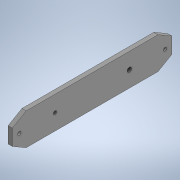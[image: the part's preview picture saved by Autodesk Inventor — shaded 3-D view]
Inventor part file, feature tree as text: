
AUTODESK INVENTOR PART (.ipt)
format: ipt  version: 2020 (Build 240168000, 168)  size: 168,448 bytes
history: native  units: in
note: dims shown in document units (in); Inventor stores cm internally (conversion verified against a paired STEP export)
features: other x3, extrude x3, sketch x3, projected_geometry x1
ambient origin geometry x8: Origin, YZ Plane, XZ Plane, XY Plane, X Axis, Y Axis, Z Axis, Center Point
bodies: Solid1 (feature_tree)
feature tree (10):
  other  "HexWheelGuard.ipt"
  extrude  "Extrusion1"  TaperAngle=0.0deg  [1 undecoded]
  extrude  "Extrusion2"  Depth=0.3937in
  extrude  "Extrusion3"  Depth=0.3937in TaperAngle=0.0deg
  other  "Solid1::HexWheelGuard.ipt"
  other  "TaggingFeature1"
  sketch  "Sketch1"  dims[d0=0.3937in d1=0.0in d2=0.0in]
  projected_geometry  "Projected Loop1"
  sketch  "Sketch2"  dims[d3=0.3937in d4=0.0in d5=0.122in]
  sketch  "Sketch3"  dims[d6=0.122in d7=0.3937in d8=0.0in]
note: 1 required parameter value undecoded (feature->parameter linkage not recoverable at this tier; creation-order binding heuristic only, values carry confidence <= 0.55)
